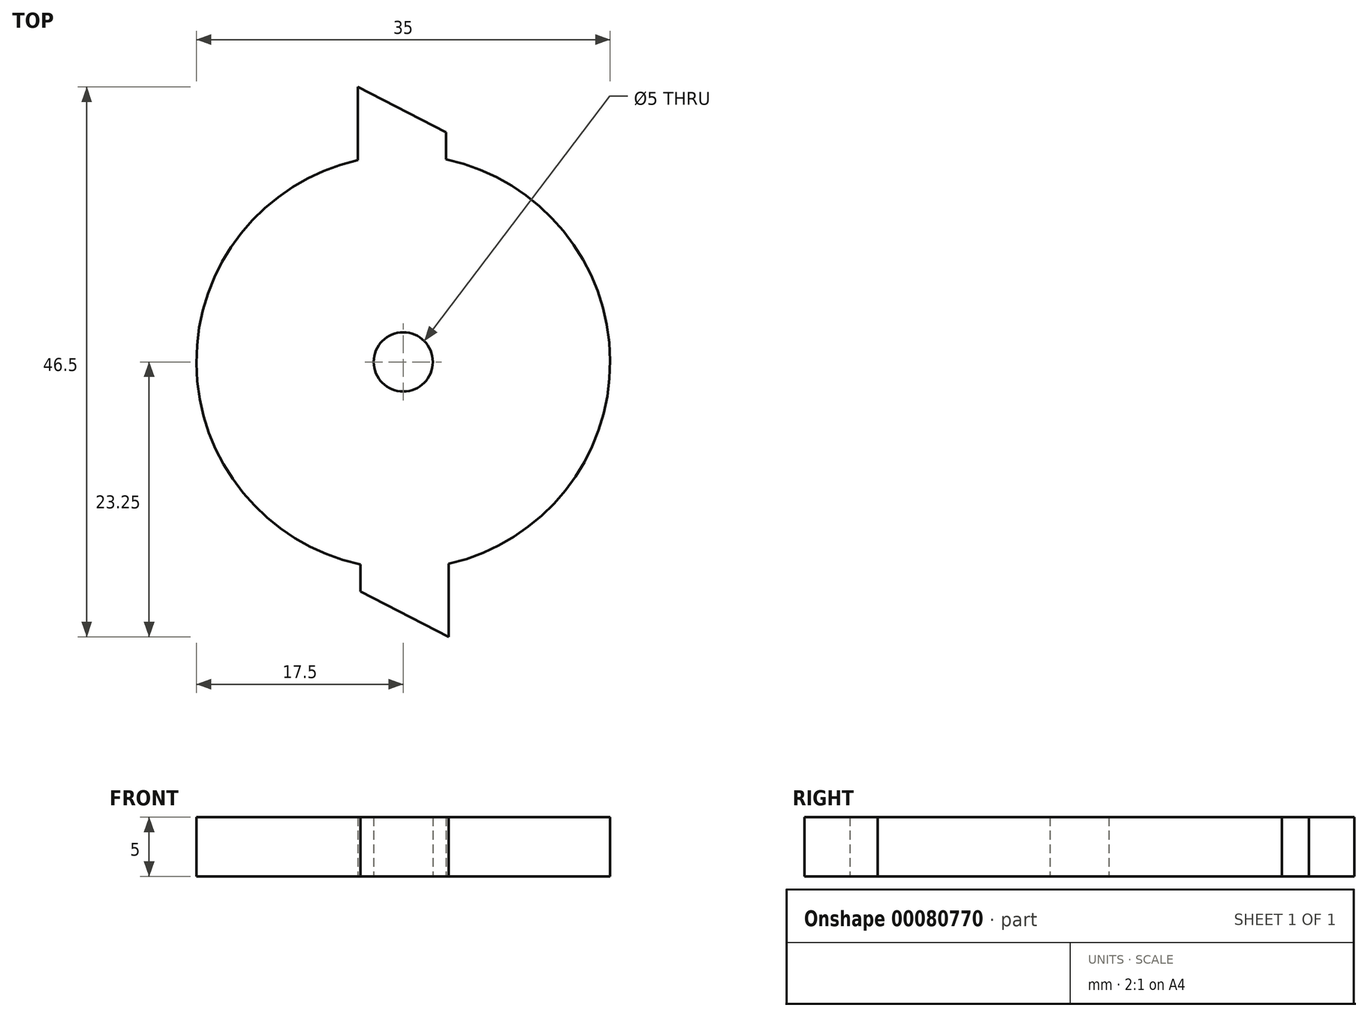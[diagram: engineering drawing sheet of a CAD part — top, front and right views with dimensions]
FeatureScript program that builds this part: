
annotation { "Feature Type Name" : "Feature", "Feature Type Description" : "" }
export const myFeature = defineFeature(function(context is Context, id is Id, definition is map)
    precondition{}
    {
        {
            var Q0;
            Q0=qCreatedBy(makeId("Top.planeOp"),FACE);
            var sketch = newSketch(context, id + "F0", { "sketchPlane" : qUnion([Q0])});
            skCircle(sketch, "E0", {"center": v(0, 0) * mm, "radius": 17.5 * mm});
            skLineSegment(sketch, "E1", {"start": v(-3.86, 17.07) * mm, "end": v(-3.86, 23.25) * mm});
            skLineSegment(sketch, "E2", {"start": v(-3.86, 23.25) * mm, "end": v(3.62, 19.4) * mm});
            skLineSegment(sketch, "E3", {"start": v(3.62, 19.4) * mm, "end": v(3.62, 17.12) * mm});
            skLineSegment(sketch, "E4.1.0", {"start": v(3.86, -23.25) * mm, "end": v(-3.62, -19.4) * mm});
            skLineSegment(sketch, "E4.1.1", {"start": v(3.86, -17.07) * mm, "end": v(3.86, -23.25) * mm});
            skLineSegment(sketch, "E4.1.2", {"start": v(-3.62, -19.4) * mm, "end": v(-3.62, -17.12) * mm});
            skCircle(sketch, "E5", {"center": v(0, 0) * mm, "radius": 2.5 * mm});
            skPoint(sketch, "E6.2.internal.snap0", {"position": v(-0.12, 21.33) * mm});
            skSolve(sketch);
        }
        {
            var Q0;
            {var subQ0=sQuery(id+"F0.wireOp",EDGE,"E0");var subQ1=makeQuery(id+"F0.imprint","INTERSECT",VERTEX,{"derivedFrom":[subQ0,sQuery(id+"F0.wireOp",EDGE,"E1")]});Q0=makeQuery(id+"F0.imprint","IMPRINT",FACE,{"disambiguationData":[TD([[makeQuery(id+"F0.imprint","IMPRINT",EDGE,{"disambiguationData":[TD([[subQ1,1.0]])],"derivedFrom":subQ0}),1.0]])]});}
            var Q1;
            {var subQ0=sQuery(id+"F0.wireOp",EDGE,"E1");Q1=makeQuery(id+"F0.imprint","IMPRINT",FACE,{"disambiguationData":[TD([[makeQuery(id+"F0.imprint","IMPRINT",EDGE,{"derivedFrom":subQ0}),-1.0]])]});}
            var Q2;
            Q2=makeQuery(id+"F0.imprint","IMPRINT",FACE,{"disambiguationData":[TD([[makeQuery(id+"F0.imprint","IMPRINT",EDGE,{"derivedFrom":sQuery(id+"F0.wireOp",EDGE,"E4.1.0")}),-1.0]])]});
            extrude(context, id + "F1", {"entities" : qUnion([Q0, Q1, Q2]), "depth" : 5 * mm});
        }
    });
